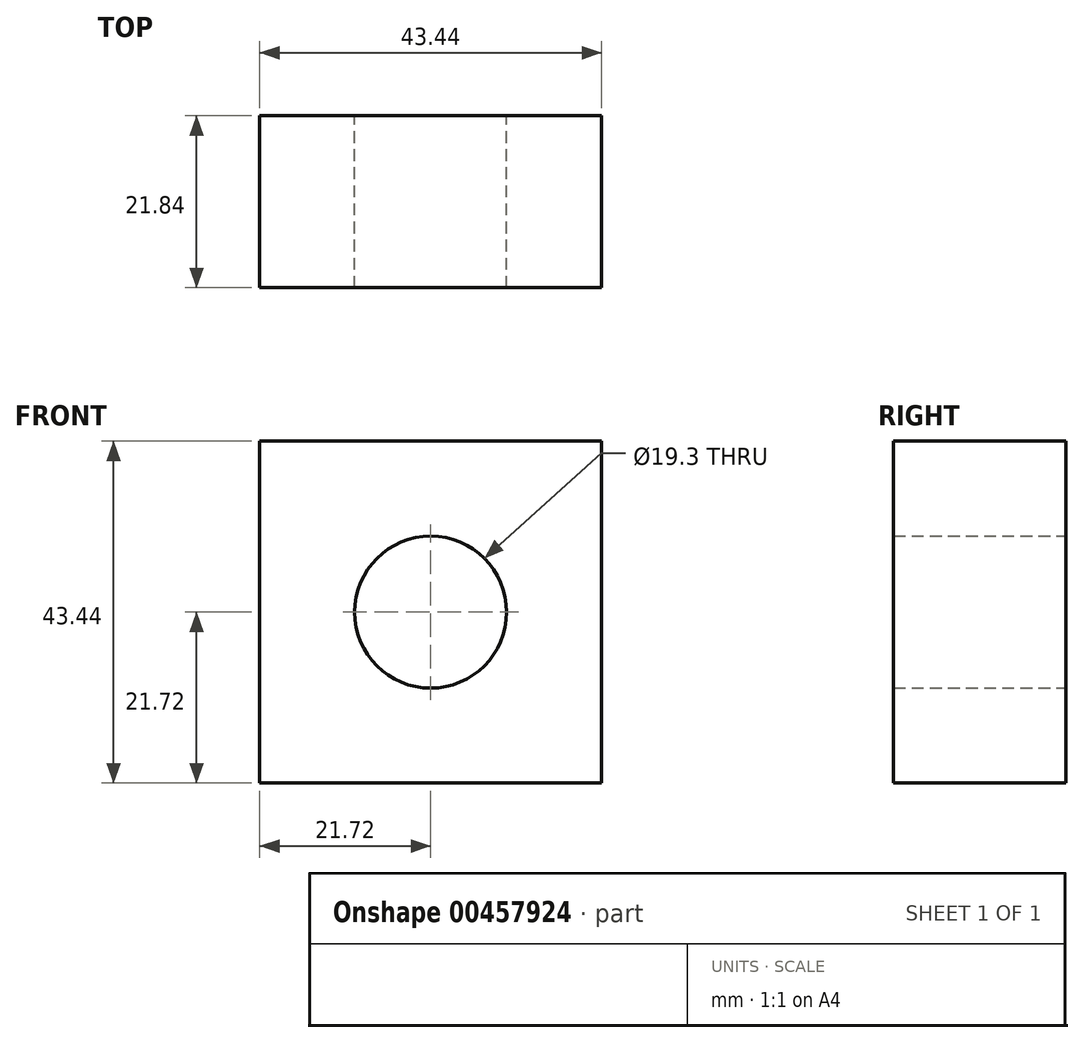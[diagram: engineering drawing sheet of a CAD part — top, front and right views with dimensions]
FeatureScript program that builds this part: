
annotation { "Feature Type Name" : "Feature", "Feature Type Description" : "" }
export const myFeature = defineFeature(function(context is Context, id is Id, definition is map)
    precondition{}
    {
        {
            var Q0;
            Q0=qCreatedBy(makeId("Front.planeOp"),FACE);
            var sketch = newSketch(context, id + "F0", { "sketchPlane" : qUnion([Q0])});
            skLineSegment(sketch, "E0.bottom", {"start": v(21.72, 21.72) * mm, "end": v(-21.72, 21.72) * mm});
            skLineSegment(sketch, "E0.top", {"start": v(21.72, -21.72) * mm, "end": v(-21.72, -21.72) * mm});
            skLineSegment(sketch, "E0.left", {"start": v(21.72, 21.72) * mm, "end": v(21.72, -21.72) * mm});
            skLineSegment(sketch, "E0.right", {"start": v(-21.72, 21.72) * mm, "end": v(-21.72, -21.72) * mm});
            skPoint(sketch, "E0.middle", {"position": v(0, 0) * mm});
            skCircle(sketch, "E1", {"center": v(0, 0) * mm, "radius": 9.65 * mm});
            skSolve(sketch);
        }
        {
            var Q0;
            Q0 = qSketchRegion(id + "F0", true);
            extrude(context, id + "F1", {"entities" : qUnion([Q0]), "depth" : 21.84 * mm});
        }
    });
